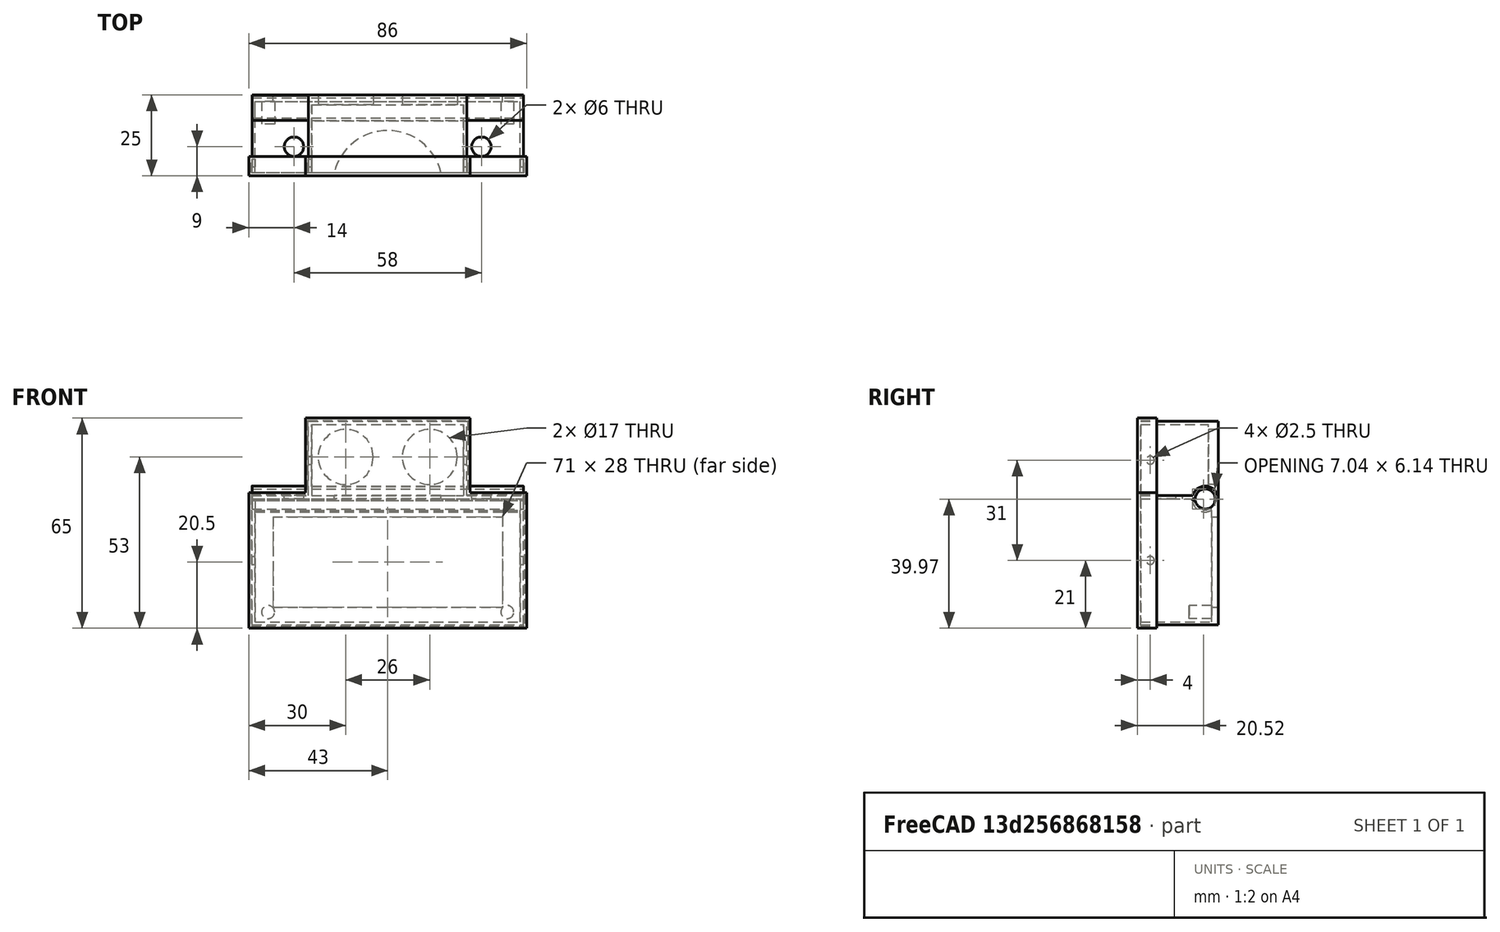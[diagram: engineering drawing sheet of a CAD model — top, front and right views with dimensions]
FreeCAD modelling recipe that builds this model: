
FCSTD DOCUMENT  (FreeCAD 0.16R6703 (Git))
Label: LCD_Ardunio_holder_v2
License: CreativeCommons Attribution-ShareAlike
LicenseURL: http://creativecommons.org/licenses/by-sa/4.0/
objects: Part::Cylinder×11, Part::Box×10, Part::Cut×9, Part::MultiFuse×5
note: 35 computed .brp shape members not serialized (recipe doc carries the construction recipe); baked Part::Feature solids carry a one-line shape summary decoded from their .brp

FEATURE [Part::Cylinder] Cylinder  label="ultraSoun1"
  Angle = 360
  Height = 20
  Placement = pos=(-13,10,0) rot=(1,0,0;1.5708rad)
  Radius = 8.5
FEATURE [Part::Cylinder] Cylinder001  label="ultraSoun002"
  Angle = 360
  Height = 20
  Placement = pos=(13,10,0) rot=(1,0,0;1.5708rad)
  Radius = 8.5
FEATURE [Part::Box] Box  label="base"
  Height = 24
  Length = 49
  Placement = pos=(-24.5,-15,-12) rot=(0,0,1;0rad)
  Width = 24
FEATURE [Part::MultiFuse] Fusion  label="2xUltrasonidos"
  Placement = pos=(0,0,1) rot=(0,0,1;0rad)
  Shapes = -> [Cylinder,Cylinder001]
FEATURE [Part::Box] Box001  label="recote base"
  Height = 23
  Length = 47
  Placement = pos=(-23.5,-16,-12) rot=(0,0,1;0rad)
  Width = 22
FEATURE [Part::Cut] Cut  label="base botones"
  Base = -> Box
  Tool = -> Box001
FEATURE [Part::Cut] Cut001  label="Botones"
  Base = -> Cut
  Tool = -> Fusion
FEATURE [Part::Cylinder] Cylinder002  label="recorte central eje"
  Angle = 360
  Height = 84
  Placement = pos=(-42,5,-12) rot=(0,1,0;1.5708rad)
  Radius = 3.1
FEATURE [Part::Cylinder] Cylinder003  label="eje_central"
  Angle = 360
  Height = 84
  Placement = pos=(-42,5,-12) rot=(0,1,0;1.5708rad)
  Radius = 4
FEATURE [Part::Box] Box002  label="recorte eje"
  Height = 0.5
  Length = 84
  Placement = pos=(-42,1,-12.5) rot=(0,0,1;0rad)
  Width = 3
FEATURE [Part::Cylinder] Cylinder004  label="recorte tornillos tapa"
  Angle = 360
  Height = 50
  Placement = pos=(-25,-12,0) rot=(0,1,0;1.5708rad)
  Radius = 1.25
FEATURE [Part::Cylinder] Cylinder005  label="recorte cables"
  Angle = 360
  Height = 10
  Placement = pos=(29,-7,-17) rot=(0,0,1;0rad)
  Radius = 3
FEATURE [Part::Box] Box003  label="baseLCD"
  Height = 40
  Length = 84
  Placement = pos=(-42,-15,-51) rot=(0,0,1;0rad)
  Width = 24
FEATURE [Part::Box] Box004  label="recorte_baseLCD"
  Height = 38
  Length = 82
  Placement = pos=(-41,-17,-50) rot=(0,0,1;0rad)
  Width = 24
FEATURE [Part::Cut] Cut002
  Base = -> Box003
  Tool = -> Box004
FEATURE [Part::Box] Box005  label="recorte_LCD"
  Height = 28
  Length = 71
  Placement = pos=(-35.5,-14,-45.5) rot=(0,0,1;0rad)
  Width = 24
FEATURE [Part::Cut] Cut003  label="base lcd"
  Base = -> Cut002
  Tool = -> Box005
FEATURE [Part::Cylinder] Cylinder006  label="soporte_lcd_1"
  Angle = 360
  Height = 8
  Placement = pos=(-37,8,-47) rot=(1,0,0;1.5708rad)
  Radius = 2
FEATURE [Part::Cylinder] Cylinder007  label="recorte pasos"
  Angle = 360
  Height = 6
  Placement = pos=(0,-19,-16) rot=(0,0,1;0rad)
  Radius = 17
FEATURE [Part::Cylinder] Cylinder008  label="soporte_lcd_002"
  Angle = 360
  Height = 8
  Placement = pos=(37,8,-47) rot=(1,0,0;1.5708rad)
  Radius = 2
FEATURE [Part::MultiFuse] Fusion001
  Shapes = -> [Cut001,Cut003,Cylinder003,Cylinder008,Cylinder006]
FEATURE [Part::Cut] Cut004
  Base = -> Fusion001
  Tool = -> Cylinder007
FEATURE [Part::Cut] Cut005
  Base = -> Cut004
  Tool = -> Cylinder002
FEATURE [Part::Cut] Cut006
  Base = -> Cut005
  Tool = -> Box002
FEATURE [Part::Cylinder] Cylinder009  label="recorte tornillos tapa001"
  Angle = 360
  Height = 86
  Placement = pos=(-43,-12,-31) rot=(0,1,0;1.5708rad)
  Radius = 1.25
FEATURE [Part::Cylinder] Cylinder010  label="recorte cables001"
  Angle = 360
  Height = 10
  Placement = pos=(-29,-7,-17) rot=(0,0,1;0rad)
  Radius = 3
FEATURE [Part::MultiFuse] Fusion002
  Shapes = -> [Cylinder005,Cylinder004,Cylinder009,Cylinder010]
FEATURE [Part::Cut] Cut007  label="LCD_Arduino_holder"
  Base = -> Cut006
  Tool = -> Fusion002
FEATURE [Part::Box] Box006  label="baseLCD001"
  Height = 42
  Length = 86
  Placement = pos=(-43,-16,-52) rot=(0,0,1;0rad)
  Width = 6
FEATURE [Part::Box] Box007  label="base_bot001"
  Height = 26
  Length = 51
  Placement = pos=(-25.5,-16,-13) rot=(0,0,1;0rad)
  Width = 6
FEATURE [Part::Box] Box008  label="baseLCD002"
  Height = 40.5
  Length = 84.5
  Placement = pos=(-42.25,-15,-51.25) rot=(0,0,1;0rad)
  Width = 24
FEATURE [Part::Box] Box009  label="base_bot002"
  Height = 24.5
  Length = 49.5
  Placement = pos=(-24.75,-15,-12.25) rot=(0,0,1;0rad)
  Width = 24
FEATURE [Part::MultiFuse] Fusion003
  Shapes = -> [Box006,Box007]
FEATURE [Part::MultiFuse] Fusion004
  Shapes = -> [Box008,Box009]
FEATURE [Part::Cut] Cut008  label="cover"
  Base = -> Fusion003
  Tool = -> Fusion004
